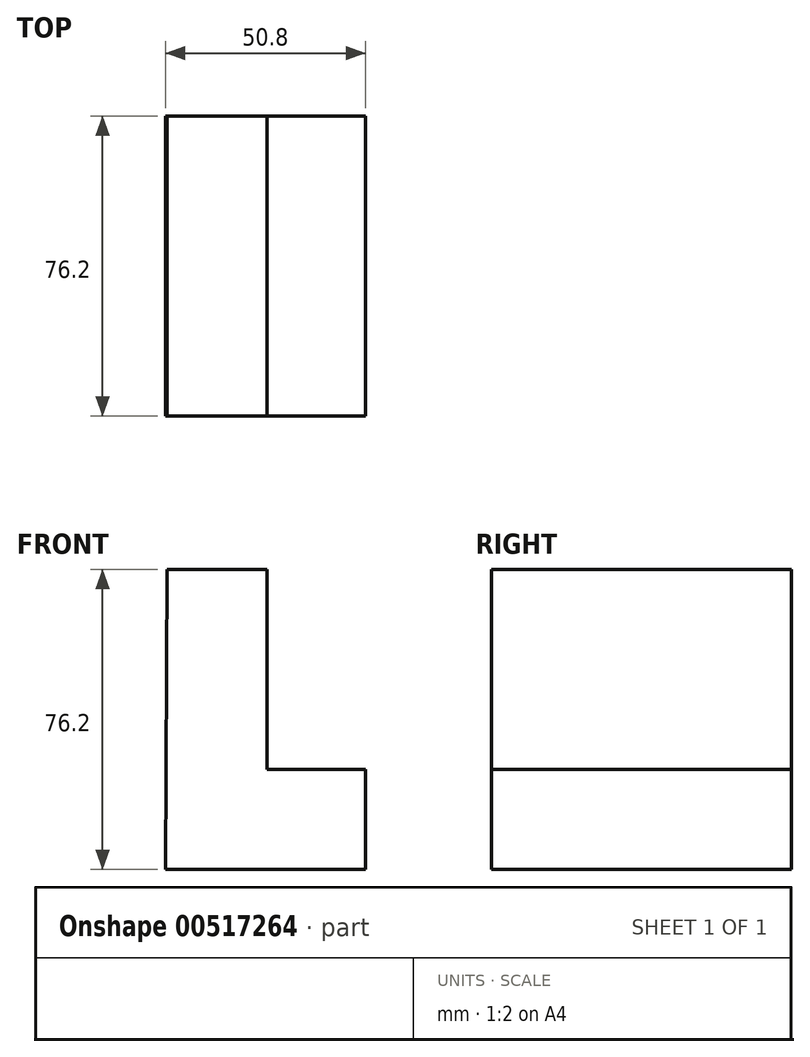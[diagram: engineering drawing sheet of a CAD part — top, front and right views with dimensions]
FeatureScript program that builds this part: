
annotation { "Feature Type Name" : "Feature", "Feature Type Description" : "" }
export const myFeature = defineFeature(function(context is Context, id is Id, definition is map)
    precondition{}
    {
        {
            var Q0;
            Q0=qCreatedBy(makeId("Front.planeOp"),FACE);
            var sketch = newSketch(context, id + "F0", { "sketchPlane" : qUnion([Q0])});
            skLineSegment(sketch, "E0", {"start": v(-34.71, -19.22) * mm, "end": v(16.09, -19.22) * mm});
            skLineSegment(sketch, "E1", {"start": v(16.09, -19.22) * mm, "end": v(16.09, 6.18) * mm});
            skLineSegment(sketch, "E2", {"start": v(16.09, 6.18) * mm, "end": v(-9.4, 6.18) * mm});
            skLineSegment(sketch, "E3", {"start": v(-8.96, 6.18) * mm, "end": v(-8.96, 56.98) * mm});
            skLineSegment(sketch, "E4", {"start": v(-8.96, 56.98) * mm, "end": v(-34.36, 56.98) * mm});
            skLineSegment(sketch, "E5", {"start": v(-34.36, 56.98) * mm, "end": v(-34.71, -19.22) * mm});
            skSolve(sketch);
        }
        {
            var Q0;
            Q0=makeQuery(id+"F0.imprint","IMPRINT",FACE,{"disambiguationData":[TD([[makeQuery(id+"F0.imprint","IMPRINT",EDGE,{"derivedFrom":sQuery(id+"F0.wireOp",EDGE,"E0")}),1.0]])]});
            extrude(context, id + "F1", {"entities" : qUnion([Q0]), "endBound" : BoundingType.SYMMETRIC, "depth" : 76.2 * mm, "offsetDistance" : 25.4 * mm});
        }
    });
